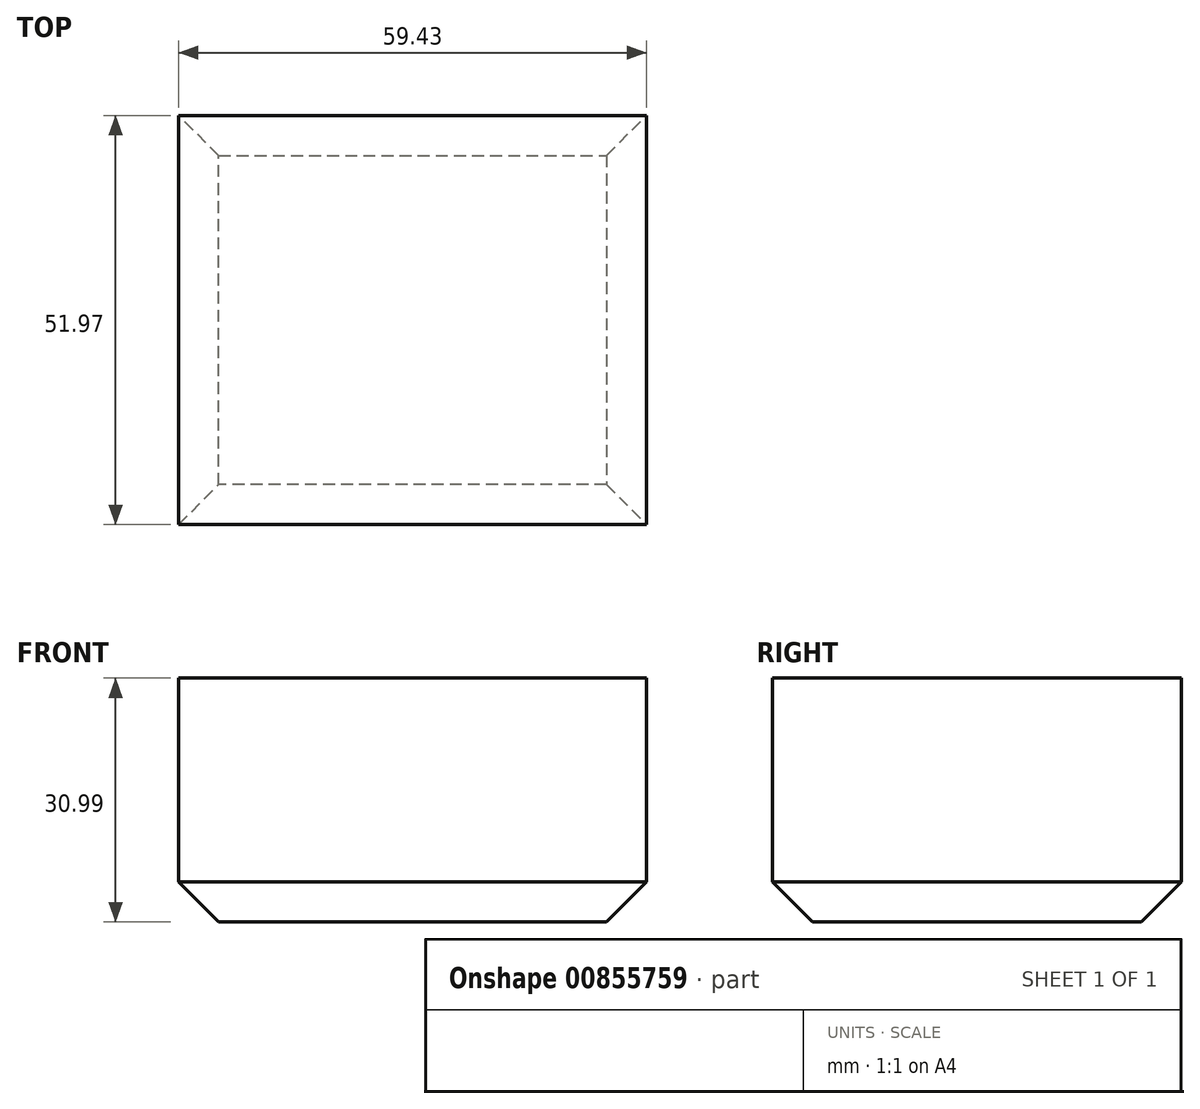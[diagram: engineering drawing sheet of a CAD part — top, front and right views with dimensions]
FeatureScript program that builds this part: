
annotation { "Feature Type Name" : "Feature", "Feature Type Description" : "" }
export const myFeature = defineFeature(function(context is Context, id is Id, definition is map)
    precondition{}
    {
        {
            var Q0;
            Q0=qCreatedBy(makeId("Top.planeOp"),FACE);
            var sketch = newSketch(context, id + "F0", { "sketchPlane" : qUnion([Q0])});
            skLineSegment(sketch, "E0.bottom", {"start": v(-30.6, -25.93) * mm, "end": v(28.84, -25.93) * mm});
            skLineSegment(sketch, "E0.top", {"start": v(-30.6, 26.04) * mm, "end": v(28.84, 26.04) * mm});
            skLineSegment(sketch, "E0.left", {"start": v(-30.6, -25.93) * mm, "end": v(-30.6, 26.04) * mm});
            skLineSegment(sketch, "E0.right", {"start": v(28.84, -25.93) * mm, "end": v(28.84, 26.04) * mm});
            skSolve(sketch);
        }
        {
            var Q0;
            Q0=makeQuery(id+"F0.imprint","IMPRINT",FACE,{"disambiguationData":[TD([[makeQuery(id+"F0.imprint","IMPRINT",EDGE,{"derivedFrom":sQuery(id+"F0.wireOp",EDGE,"E0.bottom")}),1.0]])]});
            extrude(context, id + "F1", {"entities" : qUnion([Q0]), "depth" : 30.99 * mm, "offsetDistance" : 25.4 * mm});
        }
        {
            var Q0;
            Q0=makeQuery(id+"F1.opExtrude","CAP_FACE",FACE,{"disambiguationData":[OSD([sQuery(id+"F0.wireOp",EDGE,"E0.bottom"),sQuery(id+"F0.wireOp",EDGE,"E0.top"),sQuery(id+"F0.wireOp",EDGE,"E0.left"),sQuery(id+"F0.wireOp",EDGE,"E0.right")])],"isStart":true});
            chamfer(context, id + "F2", {"entities" : qUnion([Q0]), "width" : 5.08 * mm, "tangentPropagation" : true});
        }
    });
